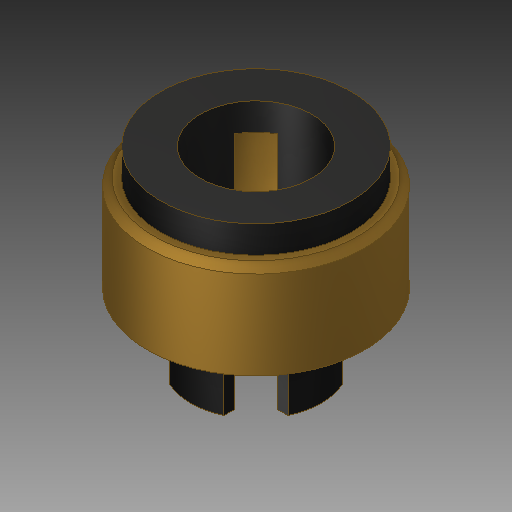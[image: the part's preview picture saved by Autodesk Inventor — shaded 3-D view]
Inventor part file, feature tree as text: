
AUTODESK INVENTOR PART (.ipt)
format: ipt  version: 2019 (Build 230136000, 136)  size: 190,976 bytes
history: native  units: mm
features: extrude x3, sketch x3, other x3, chamfer x1, pattern_circular x1
ambient origin geometry x8: Origin, YZ Plane, XZ Plane, XY Plane, X Axis, Y Axis, Z Axis, Center Point
bodies: Solid1 (feature_tree)
feature tree (11):
  extrude  "Extrusion1"  Depth=3.5mm
  chamfer  "Chamfer1"  Distance=3.5mm
  extrude  "Extrusion2"  Depth=2.0mm
  extrude  "Extrusion3"  Depth=1.0mm TaperAngle=0.0deg
  pattern_circular  "Circular Pattern1"  [2 undecoded]
  sketch  "Sketch1"  dims[d0=8.0mm d1=4.8mm d2=3.5mm d3=0.0mm]
  sketch  "Sketch2"  dims[d4=0.25mm d5=2.0mm d6=45.0deg d7=4.1mm]
  sketch  "Sketch3"  dims[d8=7.0mm d9=1.0mm d10=0.0mm d11=2.05mm d13=2.4mm d14=2.0mm d15=6.0mm d16=0.0mm d17=40.0mm d18=360.0deg]
  other  "Work Axis1"
  other  "Work Axis2"
  other  "Work Axis3"
note: 2 required parameter values undecoded (feature->parameter linkage not recoverable at this tier; creation-order binding heuristic only, values carry confidence <= 0.55)
